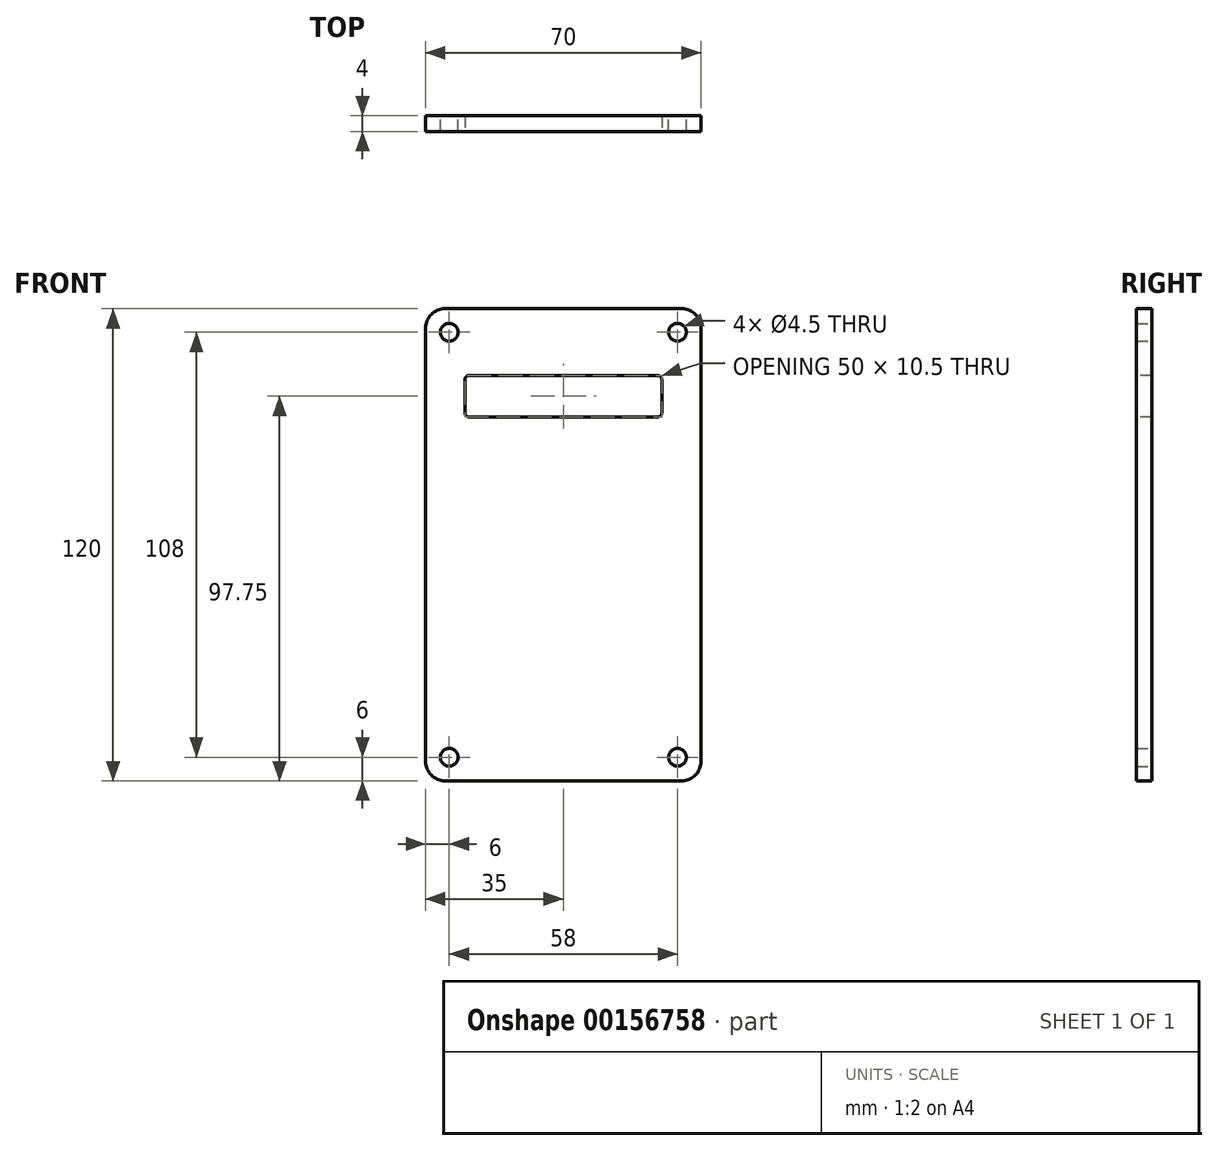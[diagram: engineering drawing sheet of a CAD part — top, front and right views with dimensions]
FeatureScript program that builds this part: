
annotation { "Feature Type Name" : "Feature", "Feature Type Description" : "" }
export const myFeature = defineFeature(function(context is Context, id is Id, definition is map)
    precondition{}
    {
        {
            var Q0;
            Q0=qCreatedBy(makeId("Front.planeOp"),FACE);
            var sketch = newSketch(context, id + "F0", { "sketchPlane" : qUnion([Q0])});
            skLineSegment(sketch, "E0.bottom", {"start": v(-35, 60) * mm, "end": v(35, 60) * mm});
            skLineSegment(sketch, "E0.top", {"start": v(-35, -60) * mm, "end": v(35, -60) * mm});
            skLineSegment(sketch, "E0.left", {"start": v(-35, 60) * mm, "end": v(-35, -60) * mm});
            skLineSegment(sketch, "E0.right", {"start": v(35, 60) * mm, "end": v(35, -60) * mm});
            skPoint(sketch, "E0.middle", {"position": v(0, 0) * mm});
            skLineSegment(sketch, "E1.bottom", {"start": v(-29, 54) * mm, "end": v(29, 54) * mm});
            skLineSegment(sketch, "E1.top", {"start": v(-29, -54) * mm, "end": v(29, -54) * mm});
            skLineSegment(sketch, "E1.left", {"start": v(-29, 54) * mm, "end": v(-29, -54) * mm});
            skLineSegment(sketch, "E1.right", {"start": v(29, 54) * mm, "end": v(29, -54) * mm});
            skCircle(sketch, "E2", {"center": v(-29, 54) * mm, "radius": 2.25 * mm});
            skCircle(sketch, "E3.MirrorC", {"center": v(29, 54) * mm, "radius": 2.25 * mm});
            skCircle(sketch, "E4.MirrorC", {"center": v(-29, -54) * mm, "radius": 2.25 * mm});
            skCircle(sketch, "E5.MirrorC", {"center": v(29, -54) * mm, "radius": 2.25 * mm});
            skSolve(sketch);
        }
        {
            var Q0;
            Q0=makeQuery(id+"F0.imprint","IMPRINT",FACE,{"disambiguationData":[TD([[makeQuery(id+"F0.imprint","IMPRINT",EDGE,{"derivedFrom":sQuery(id+"F0.wireOp",EDGE,"E0.bottom")}),-1.0]])]});
            var Q1;
            {var subQ5=sQuery(id+"F0.wireOp",EDGE,"E2");var subQ13=sQuery(id+"F0.wireOp",EDGE,"E1.bottom");var subQ14=makeQuery(id+"F0.imprint","INTERSECT",VERTEX,{"derivedFrom":[subQ13,subQ5]});Q1=makeQuery(id+"F0.imprint","IMPRINT",FACE,{"disambiguationData":[TD([[makeQuery(id+"F0.imprint","IMPRINT",EDGE,{"disambiguationData":[TD([[subQ14,-1.0]])],"derivedFrom":subQ13}),-1.0]])]});}
            extrude(context, id + "F1", {"entities" : qUnion([Q0, Q1]), "depth" : 4 * mm});
        }
        {
            var Q0;
            Q0=makeQuery(id+"F1.opExtrude","SWEPT_EDGE",EDGE,{"disambiguationData":[OSD([sQuery(id+"F0.wireOp",EDGE,"E0.bottom"),sQuery(id+"F0.wireOp",EDGE,"E0.left")])]});
            var Q1;
            Q1=makeQuery(id+"F1.opExtrude","SWEPT_EDGE",EDGE,{"disambiguationData":[OSD([sQuery(id+"F0.wireOp",EDGE,"E0.bottom"),sQuery(id+"F0.wireOp",EDGE,"E0.right")])]});
            var Q2;
            Q2=makeQuery(id+"F1.opExtrude","SWEPT_EDGE",EDGE,{"disambiguationData":[OSD([sQuery(id+"F0.wireOp",EDGE,"E0.top"),sQuery(id+"F0.wireOp",EDGE,"E0.left")])]});
            var Q3;
            Q3=makeQuery(id+"F1.opExtrude","SWEPT_EDGE",EDGE,{"disambiguationData":[OSD([sQuery(id+"F0.wireOp",EDGE,"E0.top"),sQuery(id+"F0.wireOp",EDGE,"E0.right")])]});
            fillet(context, id + "F2", {"entities" : qUnion([Q0, Q1, Q2, Q3]), "radius" : 5 * mm, "tangentPropagation" : true, "allowEdgeOverflow" : false});
        }
        {
            var Q0;
            Q0=makeQuery(id+"F1.opExtrude","CAP_FACE",FACE,{"disambiguationData":[OSD([sQuery(id+"F0.wireOp",EDGE,"E0.bottom"),sQuery(id+"F0.wireOp",EDGE,"E0.top"),sQuery(id+"F0.wireOp",EDGE,"E0.left"),sQuery(id+"F0.wireOp",EDGE,"E0.right"),sQuery(id+"F0.wireOp",EDGE,"E2"),sQuery(id+"F0.wireOp",EDGE,"E3.MirrorC"),sQuery(id+"F0.wireOp",EDGE,"E4.MirrorC"),sQuery(id+"F0.wireOp",EDGE,"E5.MirrorC")])],"isStart":false});
            var sketch = newSketch(context, id + "F3", { "sketchPlane" : qUnion([Q0])});
            skLineSegment(sketch, "E6.bottom", {"start": v(-25, 43) * mm, "end": v(25, 43) * mm});
            skLineSegment(sketch, "E6.top", {"start": v(-25, 32.5) * mm, "end": v(25, 32.5) * mm});
            skLineSegment(sketch, "E6.left", {"start": v(-25, 43) * mm, "end": v(-25, 32.5) * mm});
            skLineSegment(sketch, "E6.right", {"start": v(25, 43) * mm, "end": v(25, 32.5) * mm});
            skSolve(sketch);
        }
        {
            var Q0;
            Q0=qSketchRegion(id+"F3",true);
            extrude(context, id + "F4", {"entities" : qUnion([Q0]), "operationType" : NewBodyOperationType.REMOVE, "oppositeDirection" : true, "depth" : 25 * mm});
        }
        {
            var Q0;
            Q0=makeQuery(id+"F4.boolean.opBoolean","COPY",EDGE,{"derivedFrom":makeQuery(id+"F4.opExtrude","SWEPT_EDGE",EDGE,{"disambiguationData":[OSD([sQuery(id+"F3.wireOp",EDGE,"E6.top"),sQuery(id+"F3.wireOp",EDGE,"E6.left")])]})});
            var Q1;
            Q1=makeQuery(id+"F4.boolean.opBoolean","COPY",EDGE,{"derivedFrom":makeQuery(id+"F4.opExtrude","SWEPT_EDGE",EDGE,{"disambiguationData":[OSD([sQuery(id+"F3.wireOp",EDGE,"E6.bottom"),sQuery(id+"F3.wireOp",EDGE,"E6.left")])]})});
            var Q2;
            Q2=makeQuery(id+"F4.boolean.opBoolean","COPY",EDGE,{"derivedFrom":makeQuery(id+"F4.opExtrude","SWEPT_EDGE",EDGE,{"disambiguationData":[OSD([sQuery(id+"F3.wireOp",EDGE,"E6.bottom"),sQuery(id+"F3.wireOp",EDGE,"E6.right")])]})});
            var Q3;
            Q3=makeQuery(id+"F4.boolean.opBoolean","COPY",EDGE,{"derivedFrom":makeQuery(id+"F4.opExtrude","SWEPT_EDGE",EDGE,{"disambiguationData":[OSD([sQuery(id+"F3.wireOp",EDGE,"E6.top"),sQuery(id+"F3.wireOp",EDGE,"E6.right")])]})});
            fillet(context, id + "F5", {"entities" : qUnion([Q0, Q1, Q2, Q3]), "radius" : 1 * mm, "tangentPropagation" : true, "allowEdgeOverflow" : false});
        }
    });
